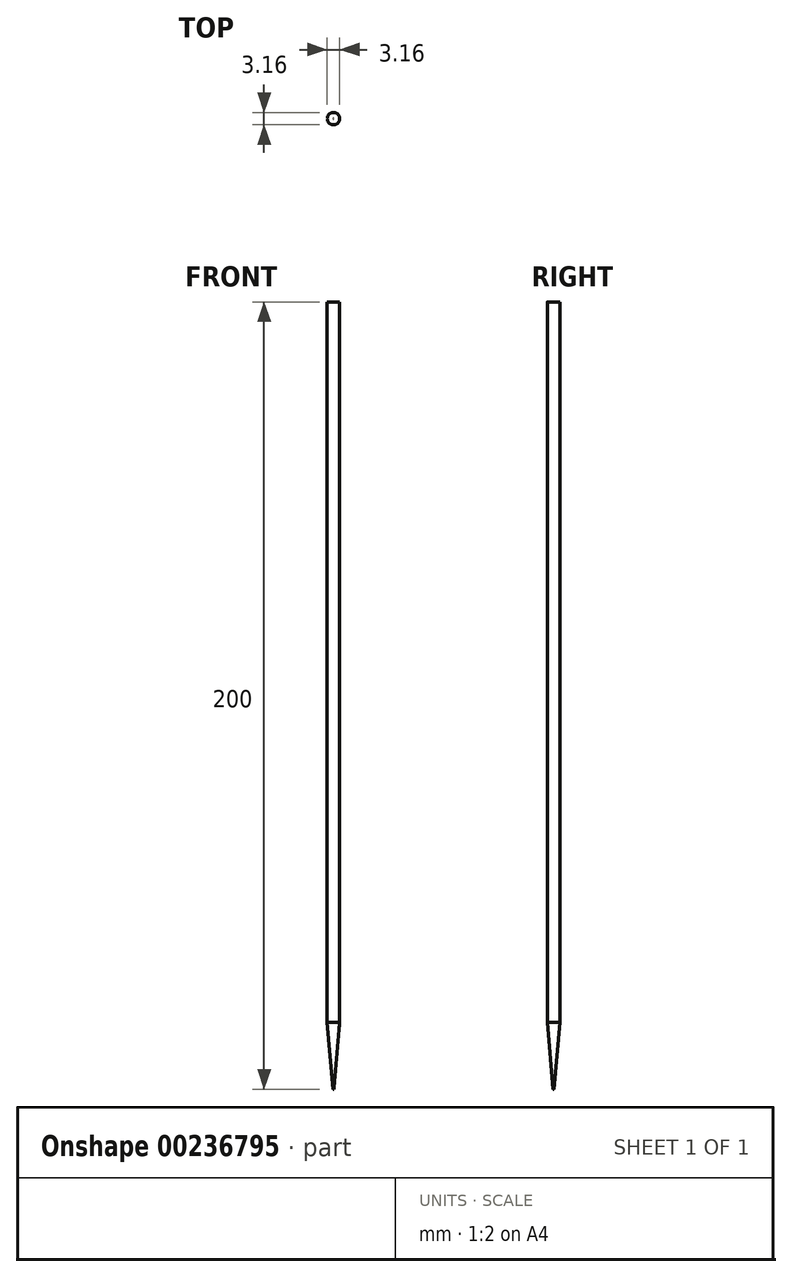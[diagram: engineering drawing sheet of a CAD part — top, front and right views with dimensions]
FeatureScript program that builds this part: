
annotation { "Feature Type Name" : "Feature", "Feature Type Description" : "" }
export const myFeature = defineFeature(function(context is Context, id is Id, definition is map)
    precondition{}
    {
        {
            var Q0;
            Q0=qCreatedBy(makeId("Top.planeOp"),FACE);
            var sketch = newSketch(context, id + "F0", { "sketchPlane" : qUnion([Q0])});
            skCircle(sketch, "E0", {"center": v(0, 0) * mm, "radius": 1.57 * mm});
            skSolve(sketch);
        }
        {
            var Q0;
            Q0 = qSketchRegion(id + "F0", true);
            extrude(context, id + "F1", {"entities" : qUnion([Q0]), "depth" : 200 * mm, "offsetDistance" : 25 * mm});
        }
        {
            var Q0;
            Q0=makeQuery(id+"F1.opExtrude","CAP_EDGE",EDGE,{"disambiguationData":[OSD([sQuery(id+"F0.wireOp",EDGE,"E0")])],"isStart":true});
            chamfer(context, id + "F2", {"entities" : qUnion([Q0]), "chamferType" : ChamferType.OFFSET_ANGLE, "width" : 17 * mm, "oppositeDirection" : false, "angle" : 5 * degree, "tangentPropagation" : true});
        }
    });
